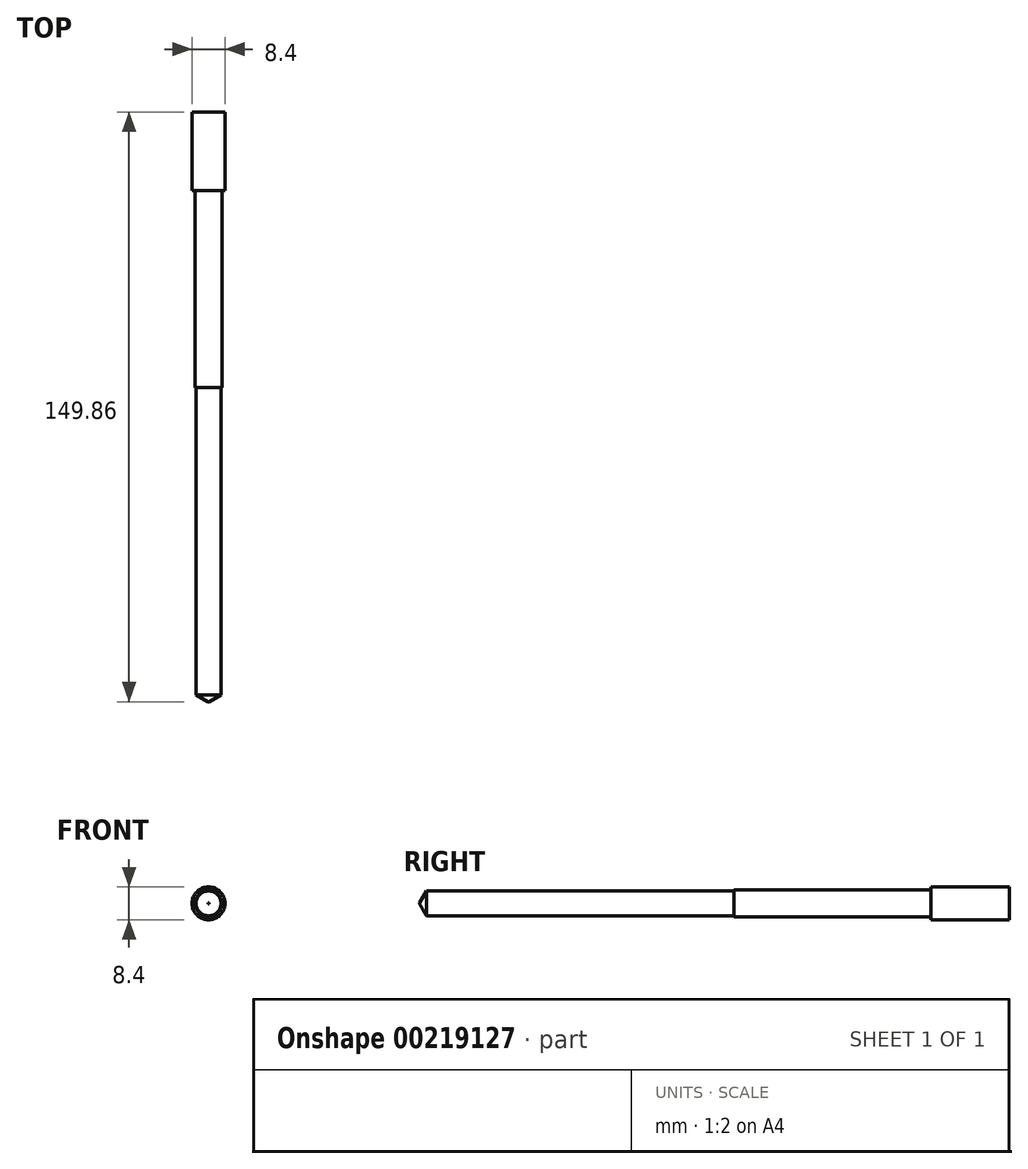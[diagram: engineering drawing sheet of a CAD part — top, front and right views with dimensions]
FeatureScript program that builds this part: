
annotation { "Feature Type Name" : "Feature", "Feature Type Description" : "" }
export const myFeature = defineFeature(function(context is Context, id is Id, definition is map)
    precondition{}
    {
        {
            var Q0;
            Q0=qCreatedBy(makeId("Front.planeOp"),FACE);
            var sketch = newSketch(context, id + "F0", { "sketchPlane" : qUnion([Q0])});
            skCircle(sketch, "E0", {"center": v(0, 0) * mm, "radius": 3.18 * mm});
            skSolve(sketch);
        }
        {
            var Q0;
            Q0=makeQuery(id+"F0.imprint","IMPRINT",FACE,{"disambiguationData":[TD([[makeQuery(id+"F0.imprint","IMPRINT",EDGE,{"derivedFrom":sQuery(id+"F0.wireOp",EDGE,"E0")}),1.0]])]});
            extrude(context, id + "F1", {"entities" : qUnion([Q0]), "depth" : 149.86 * mm});
        }
        {
            var Q0;
            Q0=makeQuery(id+"F1.opExtrude","CAP_FACE",FACE,{"disambiguationData":[OSD([sQuery(id+"F0.wireOp",EDGE,"E0")])],"isStart":false});
            chamfer(context, id + "F2", {"entities" : qUnion([Q0]), "chamferType" : ChamferType.OFFSET_ANGLE, "width" : 3.05 * mm, "oppositeDirection" : false, "angle" : 30 * degree, "tangentPropagation" : true});
        }
        {
            var Q0;
            Q0=qCreatedBy(makeId("Front.planeOp"),FACE);
            var sketch = newSketch(context, id + "F3", { "sketchPlane" : qUnion([Q0])});
            skCircle(sketch, "E1", {"center": v(0, 0) * mm, "radius": 3.4 * mm});
            skSolve(sketch);
        }
        {
            var Q0;
            Q0 = qSketchRegion(id + "F3", true);
            extrude(context, id + "F4", {"entities" : qUnion([Q0]), "operationType" : NewBodyOperationType.ADD, "depth" : 70 * mm});
        }
        {
            var Q0;
            Q0=qCreatedBy(makeId("Front.planeOp"),FACE);
            var sketch = newSketch(context, id + "F5", { "sketchPlane" : qUnion([Q0])});
            skCircle(sketch, "E2", {"center": v(0, 0) * mm, "radius": 4.2 * mm});
            skSolve(sketch);
        }
        {
            var Q0;
            Q0 = qSketchRegion(id + "F5", true);
            extrude(context, id + "F6", {"entities" : qUnion([Q0]), "operationType" : NewBodyOperationType.ADD, "depth" : 20 * mm});
        }
    });
